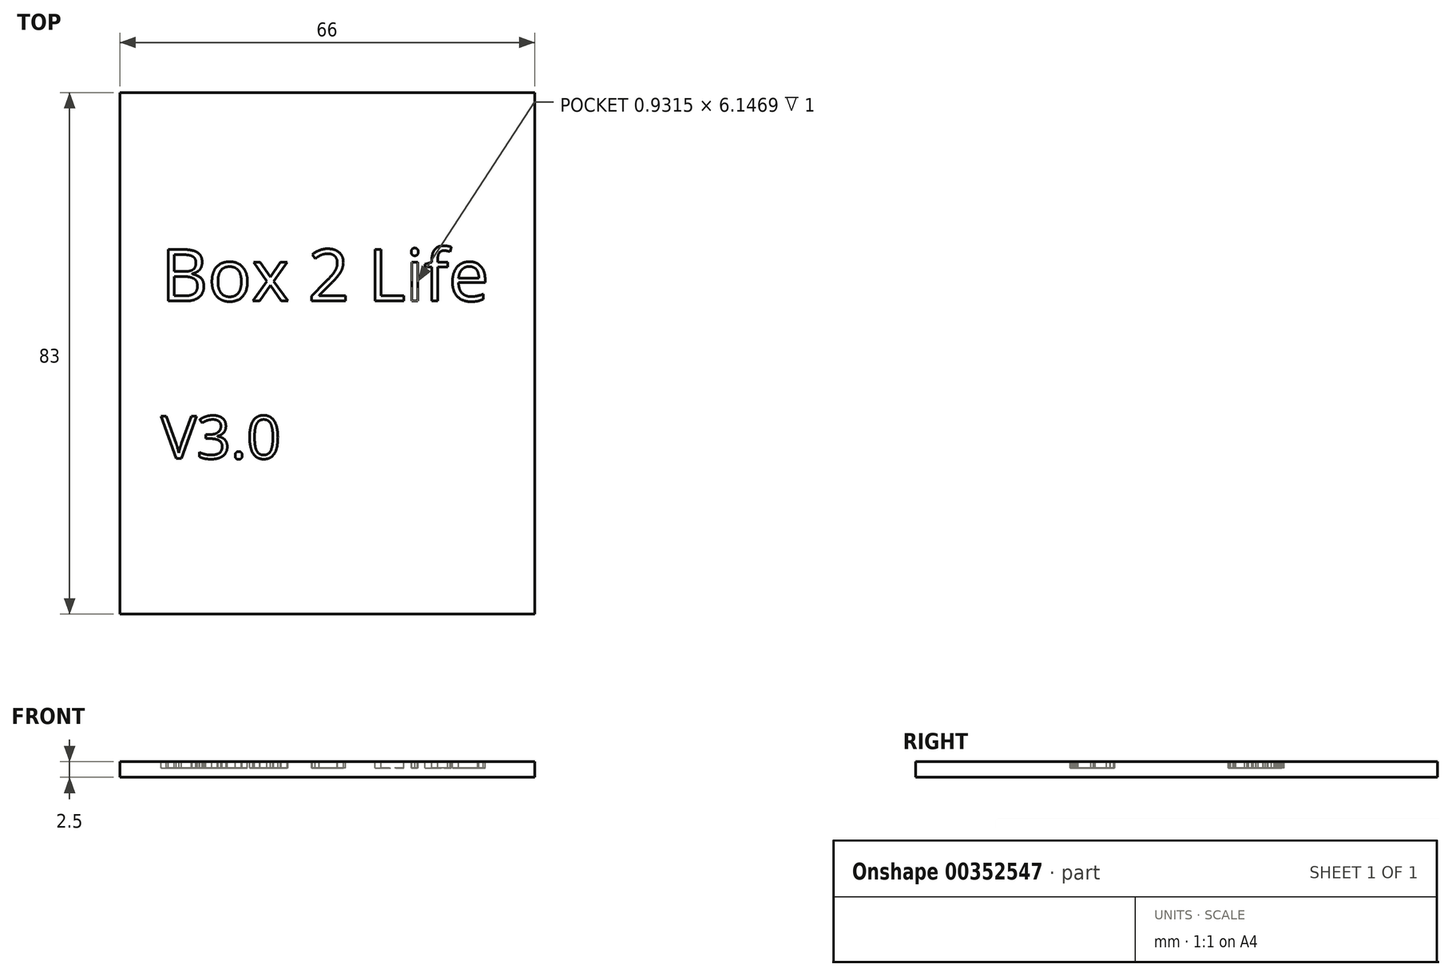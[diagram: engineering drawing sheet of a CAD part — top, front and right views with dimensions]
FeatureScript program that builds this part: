
annotation { "Feature Type Name" : "Feature", "Feature Type Description" : "" }
export const myFeature = defineFeature(function(context is Context, id is Id, definition is map)
    precondition{}
    {
        {
            var Q0;
            Q0=qCreatedBy(makeId("Top.planeOp"),FACE);
            var sketch = newSketch(context, id + "F0", { "sketchPlane" : qUnion([Q0])});
            skLineSegment(sketch, "E0.bottom", {"start": v(0, 0) * mm, "end": v(66, 0) * mm});
            skLineSegment(sketch, "E0.top", {"start": v(0, 83) * mm, "end": v(66, 83) * mm});
            skLineSegment(sketch, "E0.left", {"start": v(0, 0) * mm, "end": v(0, 83) * mm});
            skLineSegment(sketch, "E0.right", {"start": v(66, 0) * mm, "end": v(66, 83) * mm});
            skSolve(sketch);
        }
        {
            var Q0;
            Q0=qSketchRegion(id+"F0",true);
            extrude(context, id + "F1", {"entities" : qUnion([Q0]), "depth" : 2.5 * mm});
        }
        {
            var Q0;
            Q0=makeQuery(id+"F1.opExtrude","CAP_FACE",FACE,{"disambiguationData":[OSD([sQuery(id+"F0.wireOp",EDGE,"E0.bottom"),sQuery(id+"F0.wireOp",EDGE,"E0.top"),sQuery(id+"F0.wireOp",EDGE,"E0.left"),sQuery(id+"F0.wireOp",EDGE,"E0.right")])],"isStart":false});
            var sketch = newSketch(context, id + "F2", { "sketchPlane" : qUnion([Q0])});
            skText(sketch, "E1", { "text": "Box 2 Life", "fontName": "OpenSans-Regular.ttf"});
            skText(sketch, "E2", { "text": "V3.0", "fontName": "OpenSans-Regular.ttf"});
            const initialGuessF2  = {"E1": [0.00656, 0.04983, 1, 0, 0.00827], "E2": [0.00656, 0.02474, 1, 0, 0.00684]};
            skSetInitialGuess(sketch, initialGuessF2);
            skSolve(sketch);
        }
        {
            var Q0;
            Q0=qSketchRegion(id+"F2",true);
            extrude(context, id + "F3", {"entities" : qUnion([Q0]), "operationType" : NewBodyOperationType.REMOVE, "oppositeDirection" : true, "depth" : 1 * mm});
        }
    });
